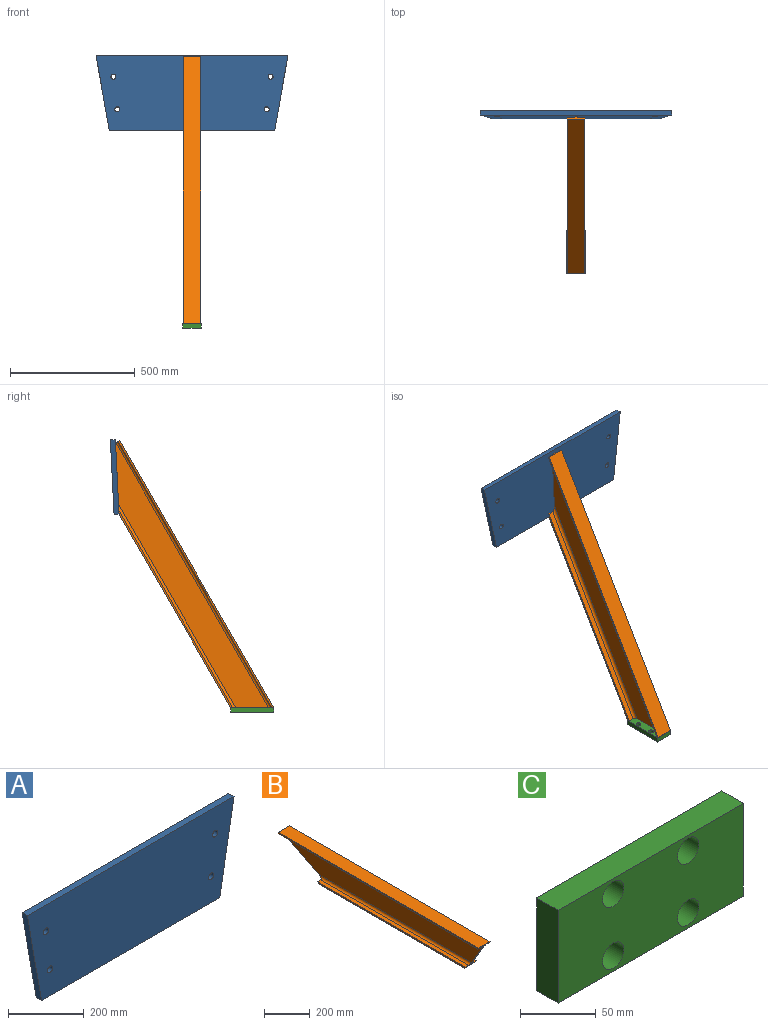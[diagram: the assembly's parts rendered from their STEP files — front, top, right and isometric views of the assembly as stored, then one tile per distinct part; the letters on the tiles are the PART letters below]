
ASSEMBLY  parts=3 mates=2
PART A: 10 faces, bbox 769.5x20x300 mm
  f0: plane 300x52.9mm, normal (0.98,0,-0.17), area 6092.6mm2, adj f1,f6,f8,f9
  f1: plane 769.54x20mm, normal (0,0,1), area 15390.7mm2, adj f0,f2,f8,f9
  f2: plane 300x52.9mm, normal (-0.98,0,-0.17), area 6092.6mm2, adj f1,f6,f8,f9
  f3: cylinder r=10mm len=20mm, axis (0,1,0), area 1256.6mm2, adj f8,f9
  f4: cylinder r=10mm len=20mm, axis (0,1,0), area 1256.6mm2, adj f8,f9
  f5: cylinder r=10mm len=20mm, axis (0,1,0), area 1256.6mm2, adj f8,f9
  f6: plane 663.74x20mm, normal (0,0,-1), area 13274.8mm2, adj f0,f2,f8,f9
  f7: cylinder r=10mm len=20mm, axis (0,1,0), area 1256.6mm2, adj f8,f9
  f8: plane 769.54x300mm, normal (0,-1,0), area 213735.1mm2, adj f0,f1,f2,f3,f4,f5,f6,f7
  f9: plane 769.54x300mm, normal (0,1,0), area 213735.1mm2, adj f0,f1,f2,f3,f4,f5,f6,f7
PART B: 19 faces, bbox 70x1235x150 mm
  f0: plane 893.58x70mm, normal (0,0,-1), area 62550.7mm2, adj f11,f12,f16,f17
  f1: plane 1224.61x114mm, normal (1,0,0), area 123480.8mm2, adj f2,f14,f16,f17,f18
  f2: cylinder r=11mm len=1230.96mm, axis (0,-1,0), area 21229.6mm2, adj f1,f3,f17,f18
  f3: plane 1230.96x21mm, normal (0,0,-1), area 25850.1mm2, adj f2,f4,f17,f18
  f4: plane 1235x7mm, normal (1,0,0), area 8630.9mm2, adj f3,f15,f17,f18
  f5: plane 1235x7mm, normal (-1,0,0), area 8630.9mm2, adj f6,f15,f17,f18
  f6: plane 1230.96x22mm, normal (0,0,-1), area 27081.1mm2, adj f5,f7,f17,f18
  f7: cylinder r=11mm len=1230.96mm, axis (0,-1,0), area 21229.6mm2, adj f6,f8,f17,f18
  f8: plane 1224.61x114mm, normal (-1,0,0), area 123480.8mm2, adj f7,f9,f16,f17,f18
  f9: cylinder r=11mm len=939.09mm, axis (0,-1,0), area 15920.3mm2, adj f8,f10,f16,f17
  f10: plane 911.28x22mm, normal (0,0,1), area 20048.1mm2, adj f9,f11,f16,f17
  f11: plane 911.28x7mm, normal (-1,0,0), area 6317mm2, adj f0,f10,f16,f17
  f12: plane 911.28x7mm, normal (1,0,0), area 6317mm2, adj f0,f13,f16,f17
  f13: plane 911.28x21mm, normal (0,0,1), area 19136.8mm2, adj f12,f14,f16,f17
  f14: cylinder r=11mm len=939.09mm, axis (0,-1,0), area 15920.3mm2, adj f1,f13,f16,f17
  f15: plane 1235x70mm, normal (0,0,1), area 86450mm2, adj f4,f5,f17,f18
  f16: plane 254.82x130.63mm, normal (0,0.46,-0.89), area 2543mm2, adj f0,f1,f8,f9,f10,f11,f12,f13
  f17: plane 150x86.6mm, normal (0,-0.87,-0.5), area 2036.7mm2, adj f0,f1,f2,f3,f4,f5,f6,f7
  f18: plane 70x19.37mm, normal (0,1,0), area 603.8mm2, adj f1,f2,f3,f4,f5,f6,f7,f8
PART C: 10 faces, bbox 173x20x75 mm
  f0: plane 173x20mm, normal (0,0,1), area 3460mm2, adj f1,f7,f8,f9
  f1: plane 75x20mm, normal (-1,0,0), area 1500mm2, adj f0,f2,f8,f9
  f2: plane 173x20mm, normal (0,0,-1), area 3460mm2, adj f1,f7,f8,f9
  f3: cylinder r=10mm len=20mm, axis (0,1,0), area 1256.6mm2, adj f8,f9
  f4: cylinder r=10mm len=20mm, axis (0,1,0), area 1256.6mm2, adj f8,f9
  f5: cylinder r=10mm len=20mm, axis (0,1,0), area 1256.6mm2, adj f8,f9
  f6: cylinder r=10mm len=20mm, axis (0,1,0), area 1256.6mm2, adj f8,f9
  f7: plane 75x20mm, normal (1,0,0), area 1500mm2, adj f0,f2,f8,f9
  f8: plane 173x75mm, normal (0,-1,0), area 11718.4mm2, adj f0,f1,f2,f3,f4,f5,f6,f7
  f9: plane 173x75mm, normal (0,1,0), area 11718.4mm2, adj f0,f1,f2,f3,f4,f5,f6,f7
PLACE A rot(axis=(0,0.02,1),180deg) t=(217.12,587.01,199.3)mm
PLACE B rot(axis=(1,0,0),60deg) t=(219.62,14.5,-761.38)mm fixed
PLACE C rot(axis=(0.58,0.58,0.58),120deg) t=(217.12,36.05,-723.88)mm
MATE fastened A.f9 <-> B.f16  axis (0,-1,0.05) through (217.12,569.54,49.99)mm
MATE fastened C.f9 <-> B.f17  axis (0,0,1) through (217.12,-50.45,-723.88)mm
